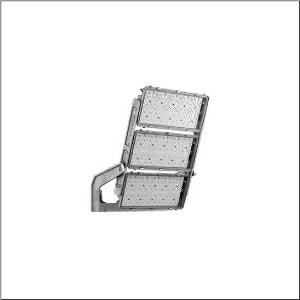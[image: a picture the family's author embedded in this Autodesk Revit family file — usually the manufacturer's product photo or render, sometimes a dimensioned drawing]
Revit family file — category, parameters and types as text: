
# Revit family: floodlight_fl_11_maxi_pro_remote___pl33t_5xa779424t01aa_a9ee
name_source: partatom
category: Lighting Fixtures
units: mm (PartAtom-declared; Revit-internal decimal feet)

## family parameters
Cut with Voids When Loaded = No
Host = Face
Light Source = No
Part Type = Normal
Room Calculation Point = No
Round Connector Dimension = Use Diameter
Shared = No

## types (1)
- --- (1 x LED, 164520 lm, 1539.3 W, 5700K)
    Apparent Load = 1539 VA
    CIE Flux Codes = 27 70 98 100 100
    Color Rendering = 90
    Color Temperature = 5700K
    Default Elevation = 1800 mm
    Description = Floodlight FL 11  maxi  pro Remote floodlight; light control with lens of PMMA; cover panel of toughened safety glass, transparent; light distribution: PL33T, asymmetric direct distribution, LEDcolour temperature: 5700K, rated luminous flux: 164.520lm, colour rendering: CRI > 90, light colour: 957; luminous efficacy: 107lm/W; brightness control: DALI 2 (1 DALI address); with terminal, 8-pole, max. 2.5mm², mains connection: 220..240V/380..400V AC, 50/60Hz, surge voltage resistance: line to ground: 10kV, ECG replaceable separately, no afterglow with DALI off / DMX off command, LED unit replaceable without ESD environment, dustproof LED module, dimming range 10..100%; 1539W floodlight with 3x LED unit of diecast aluminium, coated grey; length: 1.003mm / width: 651mm / height: 338mm; mounting bracket, of diecast aluminium, uncoated, natural, equipment: Power, protection rating (complete): IP66; insulation class (complete): insulation class I (protective earthing); certification: CE, ENEC, VDE; ball protection: ball impact resistant, impact resistance: IK07; only for outdoor installations, rated ambient temperature 10°C, permissible operating ambient temperature: -40..+30°C, permissible storage temperature: -40..+85°Cpackaging unit: 1 piece

Light Distribution: PL33T
    Height = 320 mm
    Lamp = 1 x LED
    Lamp Light Flux = 164520 lm
    Lamp Power = 1539.3 W
    Lamp count = 1
    Length = 1002 mm
    Luminous efficacy = 107 lm/W
    Manufacturer = Siteco
    ModVariant = No
    Model = 5XA779424T01AA
    Mounting Place = Ceiling
    Mounting Type = Surface mounted
    Number of Poles = 1
    OnlyDefault = Yes
    Power Factor = 1
    Product Name = Floodlight FL 11 maxi pro Remote | PL33T
    Product group = floodlight | ceiling mounted
    ProductGroupID = 301
    Protection Class = Protection class I
    Protection Degree = IP 66
    RLX_Detail_Level = 1
    RLX_Emergency_Light_Flux = 0 lm
    RLX_Emergency_Type = 0
    RLX_Emergency_Type_DB = No
    RlxData = <blob elided: 52241 chars, md5=2079b2ed>
    Socket = socket
    Standby Power = 0 W
    System Light Flux = 164520 lm
    System Power = 1539 W
    Type Comments = factory setting: luminous flux: 100 % | dim-lin: 254 | 1080 mA
    Type Image = l_1349141.jpg
    URL = http://relux.com
    VarID = @adj_079020
    Voltage = 0 V
    Weight = 0.00 kg
    Width = 655 mm

## geometry (parser evidence)
native form markers: Blend x4, Sweep x15
no freeform markers — native parametric forms only
